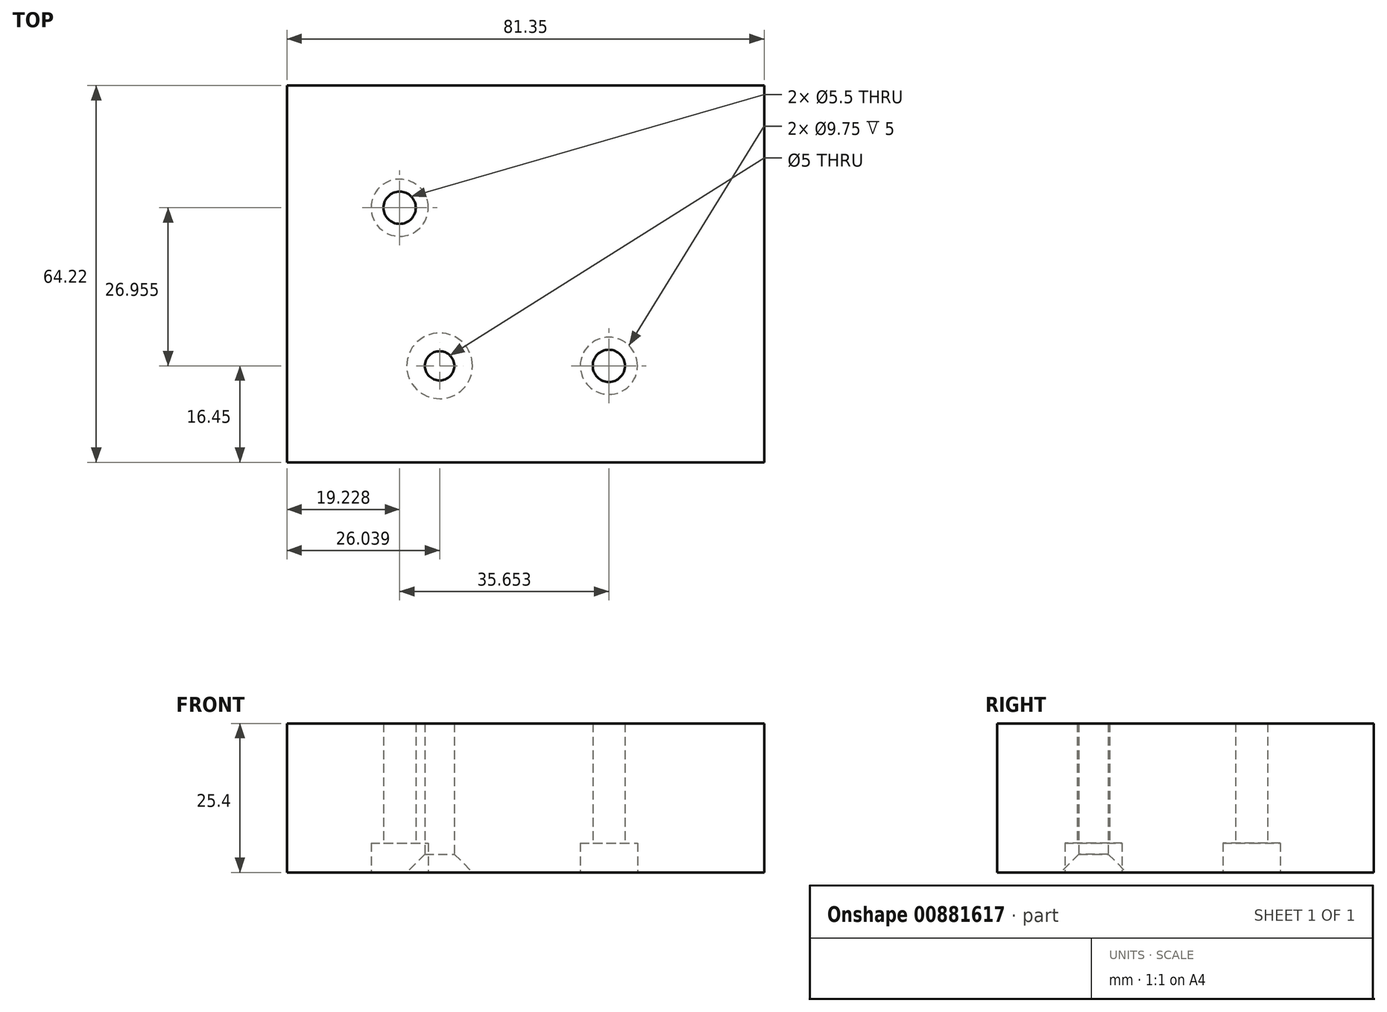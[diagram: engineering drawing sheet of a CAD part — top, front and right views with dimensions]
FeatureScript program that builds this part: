
annotation { "Feature Type Name" : "Feature", "Feature Type Description" : "" }
export const myFeature = defineFeature(function(context is Context, id is Id, definition is map)
    precondition{}
    {
        {
            var Q0;
            Q0=qCreatedBy(makeId("Top.planeOp"),FACE);
            var sketch = newSketch(context, id + "F0", { "sketchPlane" : qUnion([Q0])});
            skLineSegment(sketch, "E0.bottom", {"start": v(-60.96, 10.62) * mm, "end": v(20.4, 10.62) * mm});
            skLineSegment(sketch, "E0.top", {"start": v(-60.96, -53.6) * mm, "end": v(20.4, -53.6) * mm});
            skLineSegment(sketch, "E0.left", {"start": v(-60.96, 10.62) * mm, "end": v(-60.96, -53.6) * mm});
            skLineSegment(sketch, "E0.right", {"start": v(20.4, 10.62) * mm, "end": v(20.4, -53.6) * mm});
            skPoint(sketch, "E1", {"position": v(-41.73, -10.2) * mm});
            skPoint(sketch, "E2", {"position": v(-34.92, -37.15) * mm});
            skPoint(sketch, "E3", {"position": v(-6.08, -37.15) * mm});
            skPoint(sketch, "E4", {"position": v(-14.52, -10.2) * mm});
            skSolve(sketch);
        }
        {
            var Q0;
            Q0 = qSketchRegion(id + "F0", true);
            extrude(context, id + "F1", {"entities" : qUnion([Q0]), "depth" : 25.4 * mm, "offsetDistance" : 25.4 * mm});
        }
        {
            var Q0;
            Q0=sQuery(id+"F0.wireOp",VERTEX,"E2");
            var Q1;
            Q1=makeQuery(id+"F1.opExtrude","SWEPT_BODY",BODY,{"disambiguationData":[OSD([sQuery(id+"F0.wireOp",EDGE,"E0.bottom"),sQuery(id+"F0.wireOp",EDGE,"E0.top"),sQuery(id+"F0.wireOp",EDGE,"E0.left"),sQuery(id+"F0.wireOp",EDGE,"E0.right")])]});
            hole(context, id + "F2", {"style" : HoleStyle.C_SINK, "endStyle" : HoleEndStyle.THROUGH, "oppositeDirection" : true, "standardTappedOrClearance" : lookupTablePath({ "standard" : "ISO", "size" : "5", "type" : "Drilled" }), "standardBlindInLast" : lookupTablePath({ "standard" : "ISO", "size" : "5", "type" : "Drilled" }), "holeDiameter" : 5 * mm, "cSinkDiameter" : 11.2 * mm, "cSinkAngle" : 90 * degree, "majorDiameter" : 5 * mm, "isTappedThrough" : true, "tappedDepth" : 12 * mm, "tapClearance" : 3, "startFromSketch" : true, "locations" : qUnion([Q0]), "scope" : qUnion([Q1])});
        }
        {
            var Q0;
            Q0=sQuery(id+"F0.wireOp",VERTEX,"E1");
            var Q1;
            Q1=makeQuery(id+"F1.opExtrude","SWEPT_BODY",BODY,{"disambiguationData":[OSD([sQuery(id+"F0.wireOp",EDGE,"E0.bottom"),sQuery(id+"F0.wireOp",EDGE,"E0.top"),sQuery(id+"F0.wireOp",EDGE,"E0.left"),sQuery(id+"F0.wireOp",EDGE,"E0.right")])]});
            hole(context, id + "F3", {"style" : HoleStyle.C_BORE, "endStyle" : HoleEndStyle.THROUGH, "oppositeDirection" : true, "standardTappedOrClearance" : lookupTablePath({ "fit" : "Normal", "standard" : "ISO", "size" : "M5", "type" : "Clearance" }), "standardBlindInLast" : lookupTablePath({ "fit" : "Normal", "standard" : "ISO", "size" : "M5", "type" : "Clearance" }), "holeDiameter" : 5.5 * mm, "cBoreDiameter" : 9.75 * mm, "cBoreDepth" : 5 * mm, "majorDiameter" : 5 * mm, "isTappedThrough" : true, "tappedDepth" : 12 * mm, "tapClearance" : 3, "startFromSketch" : true, "locations" : qUnion([Q0]), "scope" : qUnion([Q1])});
        }
        {
            var Q0;
            Q0=sQuery(id+"F0.wireOp",VERTEX,"E3");
            var Q1;
            Q1=makeQuery(id+"F1.opExtrude","SWEPT_BODY",BODY,{"disambiguationData":[OSD([sQuery(id+"F0.wireOp",EDGE,"E0.bottom"),sQuery(id+"F0.wireOp",EDGE,"E0.top"),sQuery(id+"F0.wireOp",EDGE,"E0.left"),sQuery(id+"F0.wireOp",EDGE,"E0.right")])]});
            hole(context, id + "F4", {"style" : HoleStyle.C_BORE, "endStyle" : HoleEndStyle.THROUGH, "oppositeDirection" : true, "standardTappedOrClearance" : lookupTablePath({ "fit" : "Normal", "standard" : "ISO", "size" : "M5", "type" : "Clearance" }), "standardBlindInLast" : lookupTablePath({ "fit" : "Normal", "standard" : "ISO", "size" : "M5", "type" : "Clearance" }), "holeDiameter" : 5.5 * mm, "cBoreDiameter" : 9.75 * mm, "cBoreDepth" : 5 * mm, "majorDiameter" : 5 * mm, "isTappedThrough" : true, "tappedDepth" : 12 * mm, "tapClearance" : 3, "startFromSketch" : true, "locations" : qUnion([Q0]), "scope" : qUnion([Q1])});
        }
    });
